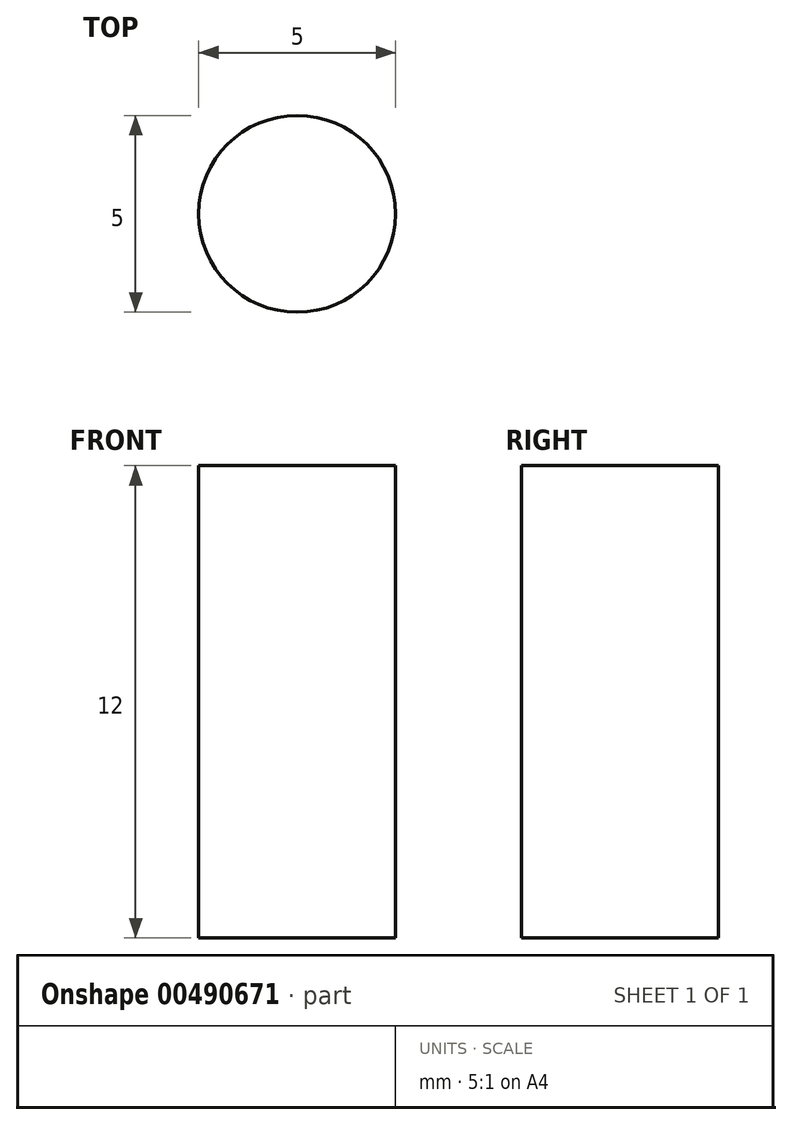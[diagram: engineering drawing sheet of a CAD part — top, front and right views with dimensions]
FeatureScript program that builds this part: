
annotation { "Feature Type Name" : "Feature", "Feature Type Description" : "" }
export const myFeature = defineFeature(function(context is Context, id is Id, definition is map)
    precondition{}
    {
        {
            var Q0;
            Q0=qCreatedBy(makeId("Top.planeOp"),FACE);
            var sketch = newSketch(context, id + "F0", { "sketchPlane" : qUnion([Q0])});
            skCircle(sketch, "E0", {"center": v(0, 0) * mm, "radius": 2.5 * mm});
            skSolve(sketch);
        }
        {
            var Q0;
            Q0=makeQuery(id+"F0.imprint","IMPRINT",FACE,{"disambiguationData":[TD([[makeQuery(id+"F0.imprint","IMPRINT",EDGE,{"derivedFrom":sQuery(id+"F0.wireOp",EDGE,"E0")}),1.0]])]});
            extrude(context, id + "F1", {"entities" : qUnion([Q0]), "depth" : 12 * mm, "offsetDistance" : 25 * mm});
        }
    });
